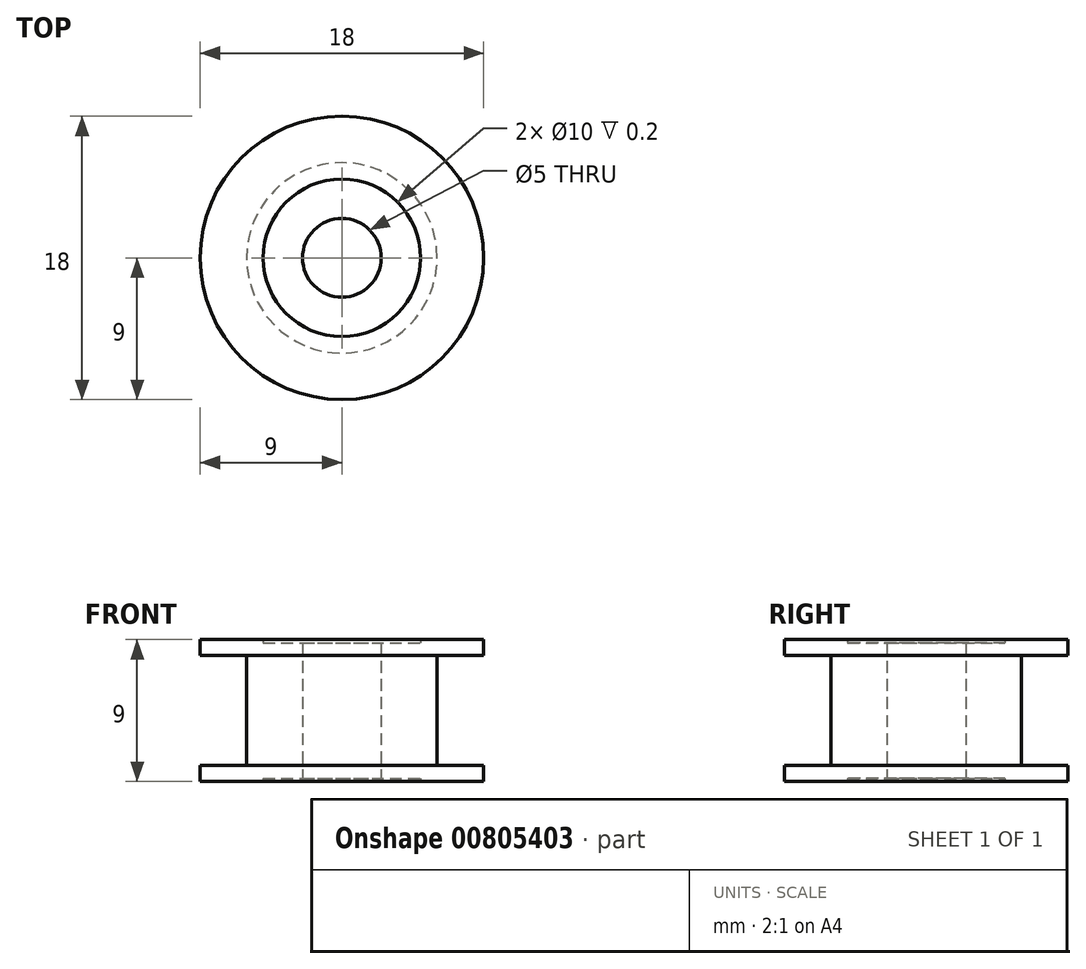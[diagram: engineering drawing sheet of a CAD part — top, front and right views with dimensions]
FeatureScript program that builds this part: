
annotation { "Feature Type Name" : "Feature", "Feature Type Description" : "" }
export const myFeature = defineFeature(function(context is Context, id is Id, definition is map)
    precondition{}
    {
        {
            var Q0;
            Q0=qCreatedBy(makeId("Front.planeOp"),FACE);
            var sketch = newSketch(context, id + "F0", { "sketchPlane" : qUnion([Q0])});
            skLineSegment(sketch, "E0", {"start": v(0, -4.5) * mm, "end": v(0, 4.5) * mm});
            skLineSegment(sketch, "E1", {"start": v(0, 4.5) * mm, "end": v(9, 4.5) * mm});
            skLineSegment(sketch, "E2", {"start": v(9, 4.5) * mm, "end": v(9, 3.5) * mm});
            skLineSegment(sketch, "E3", {"start": v(9, 3.5) * mm, "end": v(6.05, 3.5) * mm});
            skLineSegment(sketch, "E4", {"start": v(6.05, 3.5) * mm, "end": v(6.05, -3.5) * mm});
            skLineSegment(sketch, "E5", {"start": v(6.05, -3.5) * mm, "end": v(9, -3.5) * mm});
            skLineSegment(sketch, "E6", {"start": v(9, -3.5) * mm, "end": v(9, -4.5) * mm});
            skLineSegment(sketch, "E7", {"start": v(9, -4.5) * mm, "end": v(0, -4.5) * mm});
            skLineSegment(sketch, "E8", {"start": v(2.5, 4.5) * mm, "end": v(2.5, -4.5) * mm});
            skLineSegment(sketch, "E9", {"start": v(5, 4.5) * mm, "end": v(5, 4.3) * mm});
            skLineSegment(sketch, "E10", {"start": v(5, 4.3) * mm, "end": v(2.5, 4.3) * mm});
            skLineSegment(sketch, "E11.MirrorCS", {"start": v(5, -4.3) * mm, "end": v(2.5, -4.3) * mm});
            skLineSegment(sketch, "E12.MirrorCS", {"start": v(5, -4.5) * mm, "end": v(5, -4.3) * mm});
            skSolve(sketch);
        }
        {
            var Q0;
            {var subQ0=sQuery(id+"F0.wireOp",EDGE,"E2");Q0=makeQuery(id+"F0.imprint","IMPRINT",FACE,{"disambiguationData":[TD([[makeQuery(id+"F0.imprint","IMPRINT",EDGE,{"derivedFrom":subQ0}),-1.0]])]});}
            var Q1;
            Q1=sQuery(id+"F0.wireOp",EDGE,"E0");
            revolve(context, id + "F1", {"entities" : qUnion([Q0]), "axis" : qUnion([Q1]), "revolveType" : RevolveType.FULL});
        }
    });
